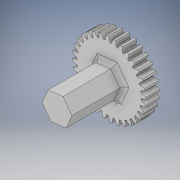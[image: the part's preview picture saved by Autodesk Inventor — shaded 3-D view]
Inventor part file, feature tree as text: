
AUTODESK INVENTOR PART (.ipt)
format: ipt  version: 2019 (Build 230136000, 136)  size: 768,512 bytes
history: native  units: in
note: dims shown in document units (in); Inventor stores cm internally (conversion verified against a paired STEP export)
features: extrude x3, projected_geometry x2, sketch x2, fillet x1, other x1
ambient origin geometry x8: Origin, YZ Plane, XZ Plane, XY Plane, X Axis, Y Axis, Z Axis, Center Point
bodies: Solid1 (feature_tree)
feature tree (9):
  extrude  "Extrusion1"  Depth=0.25in
  extrude  "Extrusion2"  Depth=0.375in
  extrude  "Extrusion3"  Depth=0.75in TaperAngle=0.0deg
  fillet  "Fillet1"  Radius=0.2in
  projected_geometry  "Projected Loop1"
  sketch  "Sketch2"  dims[d0=0.01in d1=0.0in d2=0.25in]
  sketch  "Sketch3"  dims[d3=0.2in d4=0.0in d5=0.375in d6=0.75in d7=0.0in d8=0.2in d9=0.0in d10=0.0625in]
  projected_geometry  "Projected Loop2"
  other  "bore"
